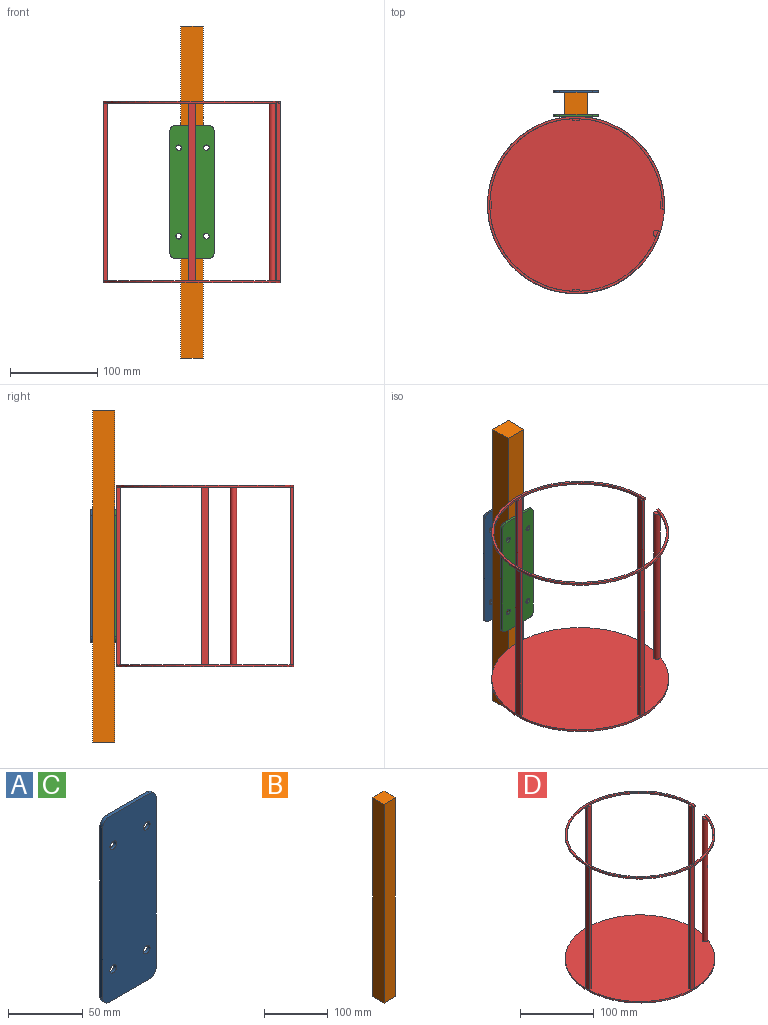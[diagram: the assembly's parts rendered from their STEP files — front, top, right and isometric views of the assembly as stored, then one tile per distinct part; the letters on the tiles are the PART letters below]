
ASSEMBLY  parts=4 mates=3
PART A: 14 faces, bbox 50.8x2.5x152.4 mm
  f0: plane 38.1x2.54mm, normal (0,0,1), area 96.8mm2, adj f1,f7,f8,f9
  f1: cylinder r=6.35mm len=6.35mm, axis (0,1,0), area 25.3mm2, adj f0,f2,f8,f9
  f2: plane 139.7x2.54mm, normal (-1,0,0), area 354.8mm2, adj f1,f3,f8,f9
  f3: cylinder r=6.35mm len=6.35mm, axis (0,1,0), area 25.3mm2, adj f2,f4,f8,f9
  f4: plane 38.1x2.54mm, normal (0,0,-1), area 96.8mm2, adj f3,f5,f8,f9
  f5: cylinder r=6.35mm len=6.35mm, axis (0,1,0), area 25.3mm2, adj f4,f6,f8,f9
  f6: plane 139.7x2.54mm, normal (1,0,0), area 354.8mm2, adj f5,f7,f8,f9
  f7: cylinder r=6.35mm len=6.35mm, axis (0,1,0), area 25.3mm2, adj f0,f6,f8,f9
  f8: plane 152.4x50.8mm, normal (0,-1,0), area 7580.6mm2, adj f0,f1,f2,f3,f4,f5,f6,f7
  f9: plane 152.4x50.8mm, normal (0,1,0), area 7580.6mm2, adj f0,f1,f2,f3,f4,f5,f6,f7
  f10: cylinder r=3.17mm len=6.35mm, axis (0,-1,0), area 50.7mm2, adj f8,f9
  f11: cylinder r=3.17mm len=6.35mm, axis (0,-1,0), area 50.7mm2, adj f8,f9
  f12: cylinder r=3.17mm len=6.35mm, axis (0,-1,0), area 50.7mm2, adj f8,f9
  f13: cylinder r=3.17mm len=6.35mm, axis (0,-1,0), area 50.7mm2, adj f8,f9
PART B: 6 faces, bbox 25.4x25.4x381 mm
  f0: plane 25.4x25.4mm, normal (0,0,-1), area 645.2mm2, adj f1,f3,f4,f5
  f1: plane 381x25.4mm, normal (1,0,0), area 9677.4mm2, adj f0,f2,f4,f5
  f2: plane 25.4x25.4mm, normal (0,0,1), area 645.2mm2, adj f1,f3,f4,f5
  f3: plane 381x25.4mm, normal (-1,0,0), area 9677.4mm2, adj f0,f2,f4,f5
  f4: plane 381x25.4mm, normal (0,-1,0), area 9677.4mm2, adj f0,f1,f2,f3
  f5: plane 381x25.4mm, normal (0,1,0), area 9677.4mm2, adj f0,f1,f2,f3
PART C: same geometry as A
PART D: 31 faces, bbox 203.2x203.2x208.3 mm
  f0: plane 203.2x203.2mm, normal (0,0,1), area 32270.1mm2, adj f1,f3,f4,f5,f6,f7,f8,f9
  f1: cylinder r=101.6mm len=203.2mm, axis (0,0,-1), area 1621.5mm2, adj f0,f2
  f2: plane 203.2x203.2mm, normal (0,0,-1), area 32429.3mm2, adj f1
  f3: plane 203.2x3.81mm, normal (-1,0,0), area 774.2mm2, adj f0,f4,f6,f20,f26
  f4: plane 203.2x7.62mm, normal (0,-1,0), area 1548.4mm2, adj f0,f3,f5,f26
  f5: plane 203.2x3.81mm, normal (1,0,0), area 774.2mm2, adj f0,f4,f6,f20,f26
  f6: plane 203.2x7.62mm, normal (0,1,0), area 1548.4mm2, adj f0,f3,f5,f20
  f7: plane 203.2x7.62mm, normal (1,0,0), area 1548.4mm2, adj f0,f8,f10,f20
  f8: plane 203.2x3.81mm, normal (0,1,0), area 774.2mm2, adj f0,f7,f9,f20,f23
  f9: plane 203.2x7.62mm, normal (-1,0,0), area 1548.4mm2, adj f0,f8,f10,f23
  f10: plane 203.2x3.81mm, normal (0,-1,0), area 774.2mm2, adj f0,f7,f9,f20,f23
  f11: plane 203.2x7.62mm, normal (0,-1,0), area 1548.4mm2, adj f0,f12,f14,f20
  f12: plane 203.2x3.81mm, normal (1,0,0), area 774.2mm2, adj f0,f11,f13,f20,f25
  f13: plane 203.2x7.62mm, normal (0,1,0), area 1548.4mm2, adj f0,f12,f14,f25
  f14: plane 203.2x3.81mm, normal (-1,0,0), area 774.2mm2, adj f0,f11,f13,f20,f25
  f15: plane 203.2x3.81mm, normal (0,1,0), area 774.2mm2, adj f0,f16,f18,f20,f28
  f16: plane 203.2x7.62mm, normal (-1,0,0), area 1548.4mm2, adj f0,f15,f17,f20
  f17: plane 203.2x3.81mm, normal (0,-1,0), area 774.2mm2, adj f0,f16,f18,f20,f28
  f18: plane 203.2x7.62mm, normal (1,0,0), area 1548.4mm2, adj f0,f15,f17,f28
  f19: cylinder r=3.7mm len=203.2mm, axis (0,0,-1), area 4726.8mm2, adj f0,f20,f24
  f20: plane 203.2x203.2mm, normal (0,0,-1), area 1453.5mm2, adj f3,f5,f6,f7,f8,f10,f11,f12
  f21: cylinder r=101.6mm len=203.2mm, axis (0,0,-1), area 1555.2mm2, adj f20,f22,f29,f30
  f22: plane 203.2x203.2mm, normal (0,0,1), area 1535.3mm2, adj f21,f27,f29,f30
  f23: plane 7.62x1.52mm, normal (0,0,1), area 11.4mm2, adj f8,f9,f10,f27
  f24: plane 7.4x6.52mm, normal (0,0,1), area 31.7mm2, adj f19,f27,f29
  f25: plane 7.62x1.52mm, normal (0,0,1), area 11.4mm2, adj f12,f13,f14,f27
  f26: plane 7.62x1.52mm, normal (0,0,1), area 11.4mm2, adj f3,f4,f5,f27
  f27: cylinder r=99.06mm len=198.12mm, axis (0,0,1), area 1515.5mm2, adj f20,f22,f23,f24,f25,f26,f28,f29
  f28: plane 7.62x1.52mm, normal (0,0,1), area 11.4mm2, adj f15,f17,f18,f27
  f29: plane 2.56x2.54mm, normal (0.13,0.99,0), area 6.6mm2, adj f20,f21,f22,f24,f27
  f30: plane 2.54x2.54mm, normal (0,-1,0), area 6.5mm2, adj f20,f21,f22,f27
PLACE A t=(-12.21,2.54,-58.58)mm
PLACE B at identity
PLACE C t=(-12.21,-25.4,-58.58)mm
PLACE D t=(0,-129.29,-104.14)mm
MATE fastened D.f6 <-> C.f8  axis (0,1,0) through (0,-27.94,0)mm
MATE fastened C.f9 <-> B.f4  axis (0,1,0) through (0,-25.4,0)mm
MATE fastened A.f8 <-> B.f5  axis (0,-1,0) through (0,0,0)mm
